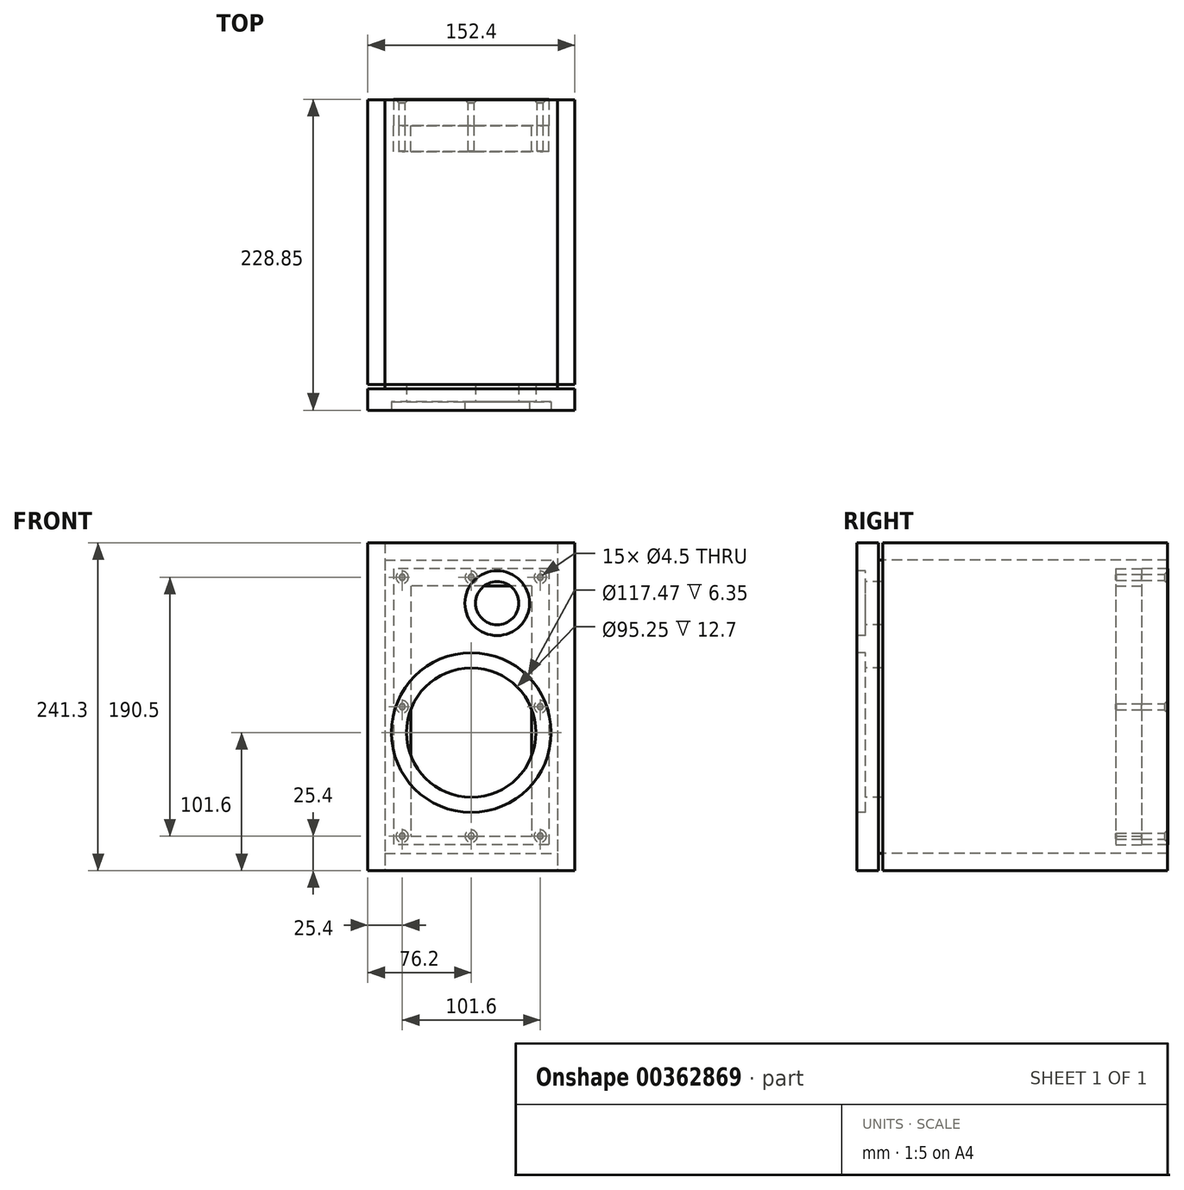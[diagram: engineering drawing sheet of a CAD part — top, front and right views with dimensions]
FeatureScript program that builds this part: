
annotation { "Feature Type Name" : "Feature", "Feature Type Description" : "" }
export const myFeature = defineFeature(function(context is Context, id is Id, definition is map)
    precondition{}
    {
        {
            var Q0;
            Q0=qCreatedBy(makeId("Front.planeOp"),FACE);
            var sketch = newSketch(context, id + "F0", { "sketchPlane" : qUnion([Q0])});
            skLineSegment(sketch, "E0.bottom", {"start": v(0, 0) * mm, "end": v(152.4, 0) * mm});
            skLineSegment(sketch, "E0.top", {"start": v(0, 241.3) * mm, "end": v(152.4, 241.3) * mm});
            skLineSegment(sketch, "E0.left", {"start": v(0, 0) * mm, "end": v(0, 241.3) * mm});
            skLineSegment(sketch, "E0.right", {"start": v(152.4, 0) * mm, "end": v(152.4, 241.3) * mm});
            skSolve(sketch);
        }
        {
            var Q0;
            Q0=makeQuery(id+"F0.imprint","IMPRINT",FACE,{"disambiguationData":[TD([[makeQuery(id+"F0.imprint","IMPRINT",EDGE,{"derivedFrom":sQuery(id+"F0.wireOp",EDGE,"E0.bottom")}),1.0]])]});
            extrude(context, id + "F1", {"entities" : qUnion([Q0]), "depth" : 19.05 * mm});
        }
        {
            var Q0;
            Q0=makeQuery(id+"F1.opExtrude","CAP_FACE",FACE,{"disambiguationData":[OSD([sQuery(id+"F0.wireOp",EDGE,"E0.bottom"),sQuery(id+"F0.wireOp",EDGE,"E0.top"),sQuery(id+"F0.wireOp",EDGE,"E0.left"),sQuery(id+"F0.wireOp",EDGE,"E0.right")])],"isStart":false});
            var sketch = newSketch(context, id + "F2", { "sketchPlane" : qUnion([Q0])});
            skCircle(sketch, "E1", {"center": v(76.2, 101.6) * mm, "radius": 58.74 * mm});
            skCircle(sketch, "E2", {"center": v(95.25, 196.85) * mm, "radius": 23.81 * mm});
            skCircle(sketch, "E3", {"center": v(76.2, 101.6) * mm, "radius": 47.63 * mm});
            skCircle(sketch, "E4", {"center": v(95.25, 196.85) * mm, "radius": 15.88 * mm});
            skSolve(sketch);
        }
        {
            var Q0;
            Q0=makeQuery(id+"F2.imprint","IMPRINT",FACE,{"disambiguationData":[TD([[makeQuery(id+"F2.imprint","IMPRINT",EDGE,{"derivedFrom":sQuery(id+"F2.wireOp",EDGE,"E2")}),1.0]])]});
            var Q1;
            Q1=makeQuery(id+"F2.imprint","IMPRINT",FACE,{"disambiguationData":[TD([[makeQuery(id+"F2.imprint","IMPRINT",EDGE,{"derivedFrom":sQuery(id+"F2.wireOp",EDGE,"E1")}),1.0]])]});
            extrude(context, id + "F3", {"entities" : qUnion([Q0, Q1]), "operationType" : NewBodyOperationType.REMOVE, "oppositeDirection" : true, "depth" : 6.35 * mm});
        }
        {
            var Q0;
            Q0=makeQuery(id+"F3.boolean.opBoolean","SPLIT",FACE,{"disambiguationData":[TD([makeQuery(id+"F3.opExtrude","SWEPT_FACE",FACE,{"disambiguationData":[OSD([sQuery(id+"F2.wireOp",EDGE,"E3")])]})])],"derivedFrom":makeQuery(id+"F1.opExtrude","CAP_FACE",FACE,{"disambiguationData":[OSD([sQuery(id+"F0.wireOp",EDGE,"E0.bottom"),sQuery(id+"F0.wireOp",EDGE,"E0.top"),sQuery(id+"F0.wireOp",EDGE,"E0.left"),sQuery(id+"F0.wireOp",EDGE,"E0.right")])],"isStart":false})});
            var Q1;
            Q1=makeQuery(id+"F3.boolean.opBoolean","SPLIT",FACE,{"disambiguationData":[TD([makeQuery(id+"F3.opExtrude","SWEPT_FACE",FACE,{"disambiguationData":[OSD([sQuery(id+"F2.wireOp",EDGE,"E4")])]})])],"derivedFrom":makeQuery(id+"F1.opExtrude","CAP_FACE",FACE,{"disambiguationData":[OSD([sQuery(id+"F0.wireOp",EDGE,"E0.bottom"),sQuery(id+"F0.wireOp",EDGE,"E0.top"),sQuery(id+"F0.wireOp",EDGE,"E0.left"),sQuery(id+"F0.wireOp",EDGE,"E0.right")])],"isStart":false})});
            extrude(context, id + "F4", {"entities" : qUnion([Q0, Q1]), "operationType" : NewBodyOperationType.REMOVE, "endBound" : BoundingType.THROUGH_ALL, "oppositeDirection" : true, "depth" : 25.4 * mm});
        }
        {
            var Q0;
            Q0=makeQuery(id+"F1.opExtrude","CAP_FACE",FACE,{"disambiguationData":[OSD([sQuery(id+"F0.wireOp",EDGE,"E0.bottom"),sQuery(id+"F0.wireOp",EDGE,"E0.top"),sQuery(id+"F0.wireOp",EDGE,"E0.left"),sQuery(id+"F0.wireOp",EDGE,"E0.right")])],"isStart":true});
            var sketch = newSketch(context, id + "F5", { "sketchPlane" : qUnion([Q0])});
            skLineSegment(sketch, "E5.bottom", {"start": v(-152.4, 241.3) * mm, "end": v(-139.7, 241.3) * mm});
            skLineSegment(sketch, "E5.top", {"start": v(-152.4, 0) * mm, "end": v(-139.7, 0) * mm});
            skLineSegment(sketch, "E5.left", {"start": v(-152.4, 241.3) * mm, "end": v(-152.4, 0) * mm});
            skLineSegment(sketch, "E5.right", {"start": v(-139.7, 241.3) * mm, "end": v(-139.7, 0) * mm});
            skLineSegment(sketch, "E6.bottom", {"start": v(0, 241.3) * mm, "end": v(-12.7, 241.3) * mm});
            skLineSegment(sketch, "E6.top", {"start": v(0, 0) * mm, "end": v(-12.7, 0) * mm});
            skLineSegment(sketch, "E6.left", {"start": v(0, 241.3) * mm, "end": v(0, 0) * mm});
            skLineSegment(sketch, "E6.right", {"start": v(-12.7, 228.6) * mm, "end": v(-12.7, 0) * mm});
            skLineSegment(sketch, "E7.bottom", {"start": v(-12.7, 0) * mm, "end": v(-139.7, 0) * mm});
            skLineSegment(sketch, "E7.top", {"start": v(-12.7, 12.7) * mm, "end": v(-139.7, 12.7) * mm});
            skLineSegment(sketch, "E7.left", {"start": v(-12.7, 0) * mm, "end": v(-12.7, 12.7) * mm});
            skLineSegment(sketch, "E7.right", {"start": v(-139.7, 0) * mm, "end": v(-139.7, 12.7) * mm});
            skLineSegment(sketch, "E8.bottom", {"start": v(-12.7, 241.3) * mm, "end": v(-139.7, 241.3) * mm});
            skLineSegment(sketch, "E8.top", {"start": v(-12.7, 228.6) * mm, "end": v(-139.7, 228.6) * mm});
            skLineSegment(sketch, "E8.left", {"start": v(-12.7, 241.3) * mm, "end": v(-12.7, 228.6) * mm});
            skLineSegment(sketch, "E8.right", {"start": v(-139.7, 241.3) * mm, "end": v(-139.7, 228.6) * mm});
            skSolve(sketch);
        }
        {
            var Q0;
            Q0=makeQuery(id+"F5.imprint","IMPRINT",FACE,{"disambiguationData":[TD([[makeQuery(id+"F5.imprint","IMPRINT",EDGE,{"derivedFrom":sQuery(id+"F5.wireOp",EDGE,"E8.bottom")}),1.0]])]});
            extrude(context, id + "F6", {"entities" : qUnion([Q0]), "depth" : 209.55 * mm});
        }
        {
            var Q0;
            Q0=makeQuery(id+"F5.imprint","IMPRINT",FACE,{"disambiguationData":[TD([[makeQuery(id+"F5.imprint","IMPRINT",EDGE,{"derivedFrom":sQuery(id+"F5.wireOp",EDGE,"E5.bottom")}),1.0]])]});
            extrude(context, id + "F7", {"entities" : qUnion([Q0]), "depth" : 209.55 * mm});
        }
        {
            var Q0;
            Q0=makeQuery(id+"F5.imprint","IMPRINT",FACE,{"disambiguationData":[TD([[makeQuery(id+"F5.imprint","IMPRINT",EDGE,{"derivedFrom":sQuery(id+"F5.wireOp",EDGE,"E6.bottom")}),1.0]])]});
            extrude(context, id + "F8", {"entities" : qUnion([Q0]), "depth" : 209.55 * mm});
        }
        {
            var Q0;
            Q0=makeQuery(id+"F5.imprint","IMPRINT",FACE,{"disambiguationData":[TD([[makeQuery(id+"F5.imprint","IMPRINT",EDGE,{"derivedFrom":sQuery(id+"F5.wireOp",EDGE,"E7.bottom")}),-1.0]])]});
            extrude(context, id + "F9", {"entities" : qUnion([Q0]), "depth" : 209.55 * mm});
        }
        {
            var Q0;
            Q0=qCreatedBy(makeId("Front.planeOp"),FACE);
            cPlane(context, id + "F10", {"entities" : qUnion([Q0]), "cplaneType" : CPlaneType.OFFSET, "offset" : 190.5 * mm, "oppositeDirection" : true, "width" : 152.4 * mm, "height" : 152.4 * mm});
        }
        {
            var Q0;
            Q0=qCreatedBy(id+"F10.planeOp",FACE);
            var sketch = newSketch(context, id + "F11", { "sketchPlane" : qUnion([Q0])});
            skLineSegment(sketch, "E9.bottom", {"start": v(133.35, 222.25) * mm, "end": v(19.05, 222.25) * mm});
            skLineSegment(sketch, "E9.top", {"start": v(133.35, 19.05) * mm, "end": v(19.05, 19.05) * mm});
            skLineSegment(sketch, "E9.left", {"start": v(133.35, 222.25) * mm, "end": v(133.35, 19.05) * mm});
            skLineSegment(sketch, "E9.right", {"start": v(19.05, 222.25) * mm, "end": v(19.05, 19.05) * mm});
            skLineSegment(sketch, "E10.0", {"start": v(120.65, 209.55) * mm, "end": v(120.65, 25.4) * mm});
            skLineSegment(sketch, "E10.1", {"start": v(120.65, 209.55) * mm, "end": v(31.75, 209.55) * mm});
            skLineSegment(sketch, "E10.2", {"start": v(31.75, 209.55) * mm, "end": v(31.75, 25.4) * mm});
            skLineSegment(sketch, "E10.3", {"start": v(31.75, 25.4) * mm, "end": v(120.65, 25.4) * mm});
            skSolve(sketch);
        }
        {
            var Q0;
            Q0=makeQuery(id+"F11.imprint","IMPRINT",FACE,{"disambiguationData":[TD([[makeQuery(id+"F11.imprint","IMPRINT",EDGE,{"derivedFrom":sQuery(id+"F11.wireOp",EDGE,"E9.bottom")}),1.0]])]});
            extrude(context, id + "F12", {"entities" : qUnion([Q0]), "depth" : 19.05 * mm});
        }
        {
            var Q0;
            Q0=qCreatedBy(id+"F10.planeOp",FACE);
            var sketch = newSketch(context, id + "F13", { "sketchPlane" : qUnion([Q0])});
            skLineSegment(sketch, "E11.bottom", {"start": v(133.35, 222.25) * mm, "end": v(19.05, 222.25) * mm});
            skLineSegment(sketch, "E11.top", {"start": v(133.35, 19.05) * mm, "end": v(19.05, 19.05) * mm});
            skLineSegment(sketch, "E11.left", {"start": v(133.35, 222.25) * mm, "end": v(133.35, 19.05) * mm});
            skLineSegment(sketch, "E11.right", {"start": v(19.05, 222.25) * mm, "end": v(19.05, 19.05) * mm});
            skLineSegment(sketch, "E12.0", {"start": v(25.4, 215.9) * mm, "end": v(25.4, 25.4) * mm, "construction": true});
            skLineSegment(sketch, "E12.1", {"start": v(127, 215.9) * mm, "end": v(25.4, 215.9) * mm, "construction": true});
            skLineSegment(sketch, "E12.2", {"start": v(127, 215.9) * mm, "end": v(127, 25.4) * mm, "construction": true});
            skLineSegment(sketch, "E12.3", {"start": v(127, 25.4) * mm, "end": v(25.4, 25.4) * mm, "construction": true});
            skPoint(sketch, "E13", {"position": v(76.2, 215.9) * mm});
            skPoint(sketch, "E14", {"position": v(127, 215.9) * mm});
            skPoint(sketch, "E15", {"position": v(127, 120.65) * mm});
            skPoint(sketch, "E16", {"position": v(127, 25.4) * mm});
            skPoint(sketch, "E17", {"position": v(76.2, 25.4) * mm});
            skPoint(sketch, "E18", {"position": v(25.4, 25.4) * mm});
            skPoint(sketch, "E19", {"position": v(25.4, 120.65) * mm});
            skPoint(sketch, "E20", {"position": v(25.4, 215.9) * mm});
            skSolve(sketch);
        }
        {
            var Q0;
            Q0=makeQuery(id+"F13.imprint","IMPRINT",FACE,{"disambiguationData":[TD([[makeQuery(id+"F13.imprint","IMPRINT",EDGE,{"derivedFrom":sQuery(id+"F13.wireOp",EDGE,"E11.bottom")}),1.0]])]});
            extrude(context, id + "F14", {"entities" : qUnion([Q0]), "oppositeDirection" : true, "depth" : 19.3 * mm});
        }
        {
            var Q0;
            Q0=makeQuery(id+"F14.opExtrude","CAP_FACE",FACE,{"disambiguationData":[OSD([sQuery(id+"F13.wireOp",EDGE,"E11.bottom"),sQuery(id+"F13.wireOp",EDGE,"E11.top"),sQuery(id+"F13.wireOp",EDGE,"E11.left"),sQuery(id+"F13.wireOp",EDGE,"E11.right")])],"isStart":false});
            var sketch = newSketch(context, id + "F15", { "sketchPlane" : qUnion([Q0])});
            skLineSegment(sketch, "E21.bottom", {"start": v(-19.05, 222.25) * mm, "end": v(-133.35, 222.25) * mm, "construction": true});
            skLineSegment(sketch, "E21.top", {"start": v(-19.05, 19.05) * mm, "end": v(-133.35, 19.05) * mm, "construction": true});
            skLineSegment(sketch, "E21.left", {"start": v(-19.05, 222.25) * mm, "end": v(-19.05, 19.05) * mm, "construction": true});
            skLineSegment(sketch, "E21.right", {"start": v(-133.35, 222.25) * mm, "end": v(-133.35, 19.05) * mm, "construction": true});
            skLineSegment(sketch, "E22.0", {"start": v(-127, 215.9) * mm, "end": v(-127, 25.4) * mm, "construction": true});
            skLineSegment(sketch, "E22.1", {"start": v(-25.4, 215.9) * mm, "end": v(-127, 215.9) * mm, "construction": true});
            skLineSegment(sketch, "E22.2", {"start": v(-25.4, 215.9) * mm, "end": v(-25.4, 25.4) * mm, "construction": true});
            skLineSegment(sketch, "E22.3", {"start": v(-25.4, 25.4) * mm, "end": v(-127, 25.4) * mm, "construction": true});
            skPoint(sketch, "E23", {"position": v(-76.2, 215.9) * mm});
            skPoint(sketch, "E24", {"position": v(-25.4, 215.9) * mm});
            skPoint(sketch, "E25", {"position": v(-25.4, 120.65) * mm});
            skPoint(sketch, "E26", {"position": v(-25.4, 25.4) * mm});
            skPoint(sketch, "E27", {"position": v(-76.2, 25.4) * mm});
            skPoint(sketch, "E28", {"position": v(-127, 25.4) * mm});
            skPoint(sketch, "E29", {"position": v(-127, 120.65) * mm});
            skPoint(sketch, "E30", {"position": v(-127, 215.9) * mm});
            skSolve(sketch);
        }
        {
            var Q0;
            Q0=sQuery(id+"F15.wireOp",VERTEX,"E23");
            var Q1;
            Q1=sQuery(id+"F15.wireOp",VERTEX,"E30");
            var Q2;
            Q2=sQuery(id+"F15.wireOp",VERTEX,"E29");
            var Q3;
            Q3=sQuery(id+"F15.wireOp",VERTEX,"E28");
            var Q4;
            Q4=sQuery(id+"F15.wireOp",VERTEX,"E27");
            var Q5;
            Q5=sQuery(id+"F15.wireOp",VERTEX,"E26");
            var Q6;
            Q6=sQuery(id+"F15.wireOp",VERTEX,"E25");
            var Q7;
            Q7=sQuery(id+"F15.wireOp",VERTEX,"E24");
            var Q8;
            Q8=makeQuery(id+"F12.opExtrude","SWEPT_BODY",BODY,{"disambiguationData":[OSD([sQuery(id+"F11.wireOp",EDGE,"E9.bottom"),sQuery(id+"F11.wireOp",EDGE,"E9.top"),sQuery(id+"F11.wireOp",EDGE,"E9.left"),sQuery(id+"F11.wireOp",EDGE,"E9.right"),sQuery(id+"F11.wireOp",EDGE,"E10.0"),sQuery(id+"F11.wireOp",EDGE,"E10.1"),sQuery(id+"F11.wireOp",EDGE,"E10.2"),sQuery(id+"F11.wireOp",EDGE,"E10.3")])]});
            var Q9;
            Q9=makeQuery(id+"F14.opExtrude","SWEPT_BODY",BODY,{"disambiguationData":[OSD([sQuery(id+"F13.wireOp",EDGE,"E11.bottom"),sQuery(id+"F13.wireOp",EDGE,"E11.top"),sQuery(id+"F13.wireOp",EDGE,"E11.left"),sQuery(id+"F13.wireOp",EDGE,"E11.right")])]});
            hole(context, id + "F16", {"style" : HoleStyle.C_SINK, "endStyle" : HoleEndStyle.BLIND, "standardTappedOrClearance" : lookupTablePath({ "standard" : "ANSI", "fit" : "Normal (ASME)", "size" : "#8", "type" : "Clearance" }), "standardBlindInLast" : lookupTablePath({ "fit" : "Free", "standard" : "ANSI", "size" : "#8", "type" : "Clearance" }), "holeDiameter" : 4.5 * mm, "cSinkDiameter" : 9.12 * mm, "cSinkAngle" : 82 * degree, "holeDepth" : 38.1 * mm, "isTappedThrough" : true, "tappedDepth" : 10.32 * mm, "tapClearance" : 3, "locations" : qUnion([Q0, Q1, Q2, Q3, Q4, Q5, Q6, Q7]), "scope" : qUnion([Q8, Q9])});
        }
        {
            var Q0;
            Q0=makeQuery(id+"F5.imprint","IMPRINT",FACE,{"disambiguationData":[TD([[makeQuery(id+"F5.imprint","IMPRINT",EDGE,{"derivedFrom":sQuery(id+"F5.wireOp",EDGE,"E8.bottom")}),1.0]])]});
            var Q1;
            Q1=makeQuery(id+"F5.imprint","IMPRINT",FACE,{"disambiguationData":[TD([[makeQuery(id+"F5.imprint","IMPRINT",EDGE,{"derivedFrom":sQuery(id+"F5.wireOp",EDGE,"E5.bottom")}),1.0]])]});
            var Q2;
            Q2=makeQuery(id+"F5.imprint","IMPRINT",FACE,{"disambiguationData":[TD([[makeQuery(id+"F5.imprint","IMPRINT",EDGE,{"derivedFrom":sQuery(id+"F5.wireOp",EDGE,"E6.bottom")}),1.0]])]});
            var Q3;
            Q3=makeQuery(id+"F5.imprint","IMPRINT",FACE,{"disambiguationData":[TD([[makeQuery(id+"F5.imprint","IMPRINT",EDGE,{"derivedFrom":sQuery(id+"F5.wireOp",EDGE,"E7.bottom")}),-1.0]])]});
            extrude(context, id + "F17", {"entities" : qUnion([Q0, Q1, Q2, Q3]), "operationType" : NewBodyOperationType.REMOVE, "oppositeDirection" : true, "depth" : 3.17 * mm});
        }
    });
